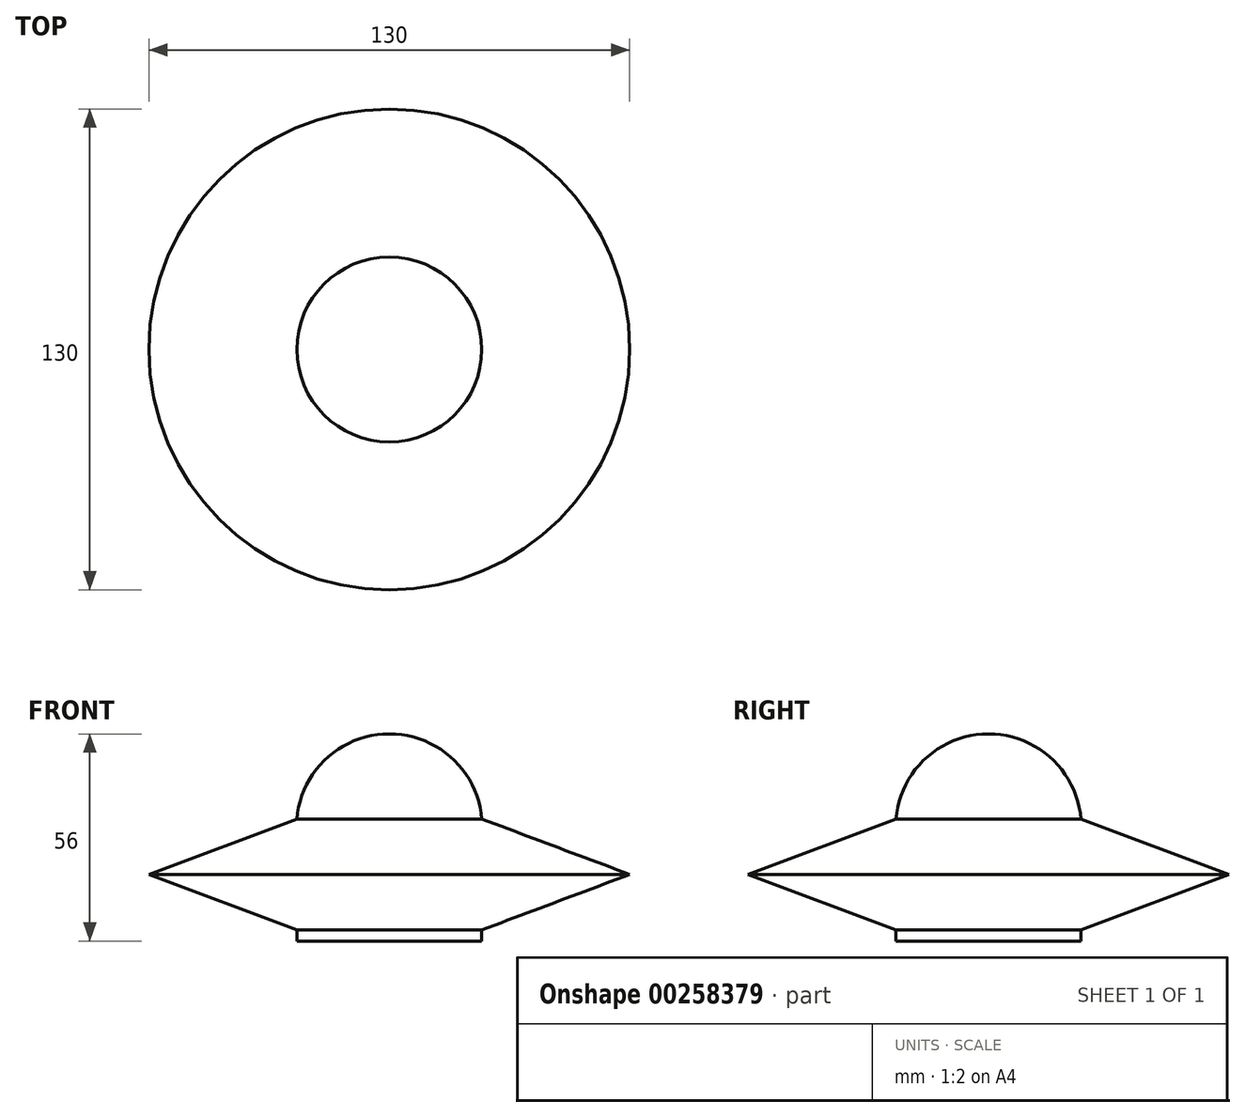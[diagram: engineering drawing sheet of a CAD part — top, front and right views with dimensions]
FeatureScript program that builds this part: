
annotation { "Feature Type Name" : "Feature", "Feature Type Description" : "" }
export const myFeature = defineFeature(function(context is Context, id is Id, definition is map)
    precondition{}
    {
        {
            var Q0;
            Q0=qCreatedBy(makeId("Top.planeOp"),FACE);
            cPlane(context, id + "F0", {"entities" : qUnion([Q0]), "cplaneType" : CPlaneType.OFFSET, "offset" : 30 * mm, "width" : 150 * mm, "height" : 150 * mm});
        }
        {
            var Q0;
            Q0=qCreatedBy(id+"F0.planeOp",FACE);
            cPlane(context, id + "F1", {"entities" : qUnion([Q0]), "cplaneType" : CPlaneType.OFFSET, "offset" : 15 * mm, "oppositeDirection" : true, "width" : 150 * mm, "height" : 150 * mm});
        }
        {
            var Q0;
            Q0=qCreatedBy(id+"F1.planeOp",FACE);
            var sketch = newSketch(context, id + "F2", { "sketchPlane" : qUnion([Q0])});
            skCircle(sketch, "E0", {"center": v(0, 0) * mm, "radius": 65 * mm});
            skSolve(sketch);
        }
        {
            var Q0;
            Q0=qCreatedBy(id+"F0.planeOp",FACE);
            var sketch = newSketch(context, id + "F3", { "sketchPlane" : qUnion([Q0])});
            skCircle(sketch, "E1", {"center": v(0, 0) * mm, "radius": 25 * mm});
            skSolve(sketch);
        }
        {
            var Q0;
            Q0=qCreatedBy(makeId("Top.planeOp"),FACE);
            var sketch = newSketch(context, id + "F4", { "sketchPlane" : qUnion([Q0])});
            skCircle(sketch, "E2", {"center": v(0, 0) * mm, "radius": 25 * mm});
            skSolve(sketch);
        }
        {
            var Q0;
            Q0=makeQuery(id+"F2.imprint","IMPRINT",FACE,{"disambiguationData":[TD([[makeQuery(id+"F2.imprint","IMPRINT",EDGE,{"derivedFrom":sQuery(id+"F2.wireOp",EDGE,"E0")}),1.0]])]});
            var Q1;
            Q1=makeQuery(id+"F3.imprint","IMPRINT",FACE,{"disambiguationData":[TD([[makeQuery(id+"F3.imprint","IMPRINT",EDGE,{"derivedFrom":sQuery(id+"F3.wireOp",EDGE,"E1")}),1.0]])]});
            loft(context, id + "F5", {"sheetProfilesArray" : [{ "sheetProfileEntities" : qUnion([Q0]) }, { "sheetProfileEntities" : qUnion([Q1]) }]});
        }
        {
            var Q1;
            Q1=makeQuery(id+"F5.opLoft","CAP_FACE",FACE,{"disambiguationData":[OSD([makeQuery(id+"F2.imprint","IMPRINT",FACE,{"disambiguationData":[TD([[makeQuery(id+"F2.imprint","IMPRINT",EDGE,{"derivedFrom":sQuery(id+"F2.wireOp",EDGE,"E0")}),1.0]])]})])],"isStart":true});
            var Q2;
            Q2=makeQuery(id+"F4.imprint","IMPRINT",FACE,{"disambiguationData":[TD([[makeQuery(id+"F4.imprint","IMPRINT",EDGE,{"derivedFrom":sQuery(id+"F4.wireOp",EDGE,"E2")}),1.0]])]});
            loft(context, id + "F6", {"operationType" : NewBodyOperationType.ADD, "sheetProfilesArray" : [{ "sheetProfileEntities" : qUnion([Q1]) }, { "sheetProfileEntities" : qUnion([Q2]) }]});
        }
        {
            var Q0;
            Q0=makeQuery(id+"F5.opLoft","CAP_FACE",FACE,{"disambiguationData":[OSD([makeQuery(id+"F3.imprint","IMPRINT",FACE,{"disambiguationData":[TD([[makeQuery(id+"F3.imprint","IMPRINT",EDGE,{"derivedFrom":sQuery(id+"F3.wireOp",EDGE,"E1")}),1.0]])]})])],"isStart":true});
            extrude(context, id + "F7", {"entities" : qUnion([Q0]), "operationType" : NewBodyOperationType.ADD, "depth" : 23 * mm});
        }
        {
            var Q0;
            Q0=makeQuery(id+"F7.opExtrude","CAP_EDGE",EDGE,{"disambiguationData":[OSD([sQuery(id+"F2.wireOp",EDGE,"E0"),sQuery(id+"F3.wireOp",EDGE,"E1")])],"isStart":false});
            fillet(context, id + "F8", {"entities" : qUnion([Q0]), "radius" : 25 * mm, "tangentPropagation" : true, "allowEdgeOverflow" : false});
        }
        {
            var Q0;
            Q0=makeQuery(id+"F6.opLoft","CAP_FACE",FACE,{"disambiguationData":[OSD([makeQuery(id+"F4.imprint","IMPRINT",FACE,{"disambiguationData":[TD([[makeQuery(id+"F4.imprint","IMPRINT",EDGE,{"derivedFrom":sQuery(id+"F4.wireOp",EDGE,"E2")}),1.0]])]})])],"isStart":true});
            extrude(context, id + "F9", {"entities" : qUnion([Q0]), "operationType" : NewBodyOperationType.ADD, "depth" : 3 * mm});
        }
    });
